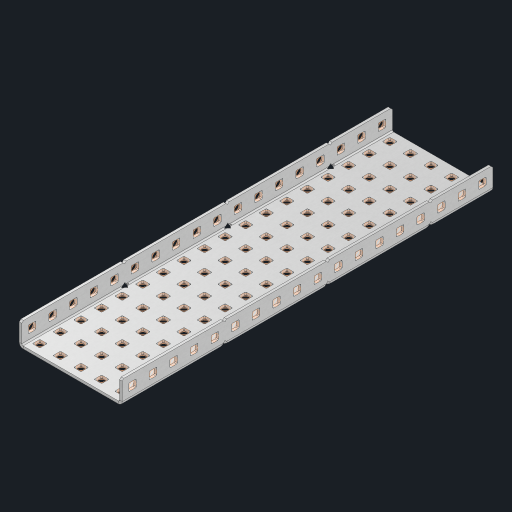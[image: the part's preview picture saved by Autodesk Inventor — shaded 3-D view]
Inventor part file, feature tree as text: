
AUTODESK INVENTOR PART (.ipt)
format: ipt  version: 2023 (Build 270158000, 158)  size: 1,542,144 bytes
history: native  units: in
note: dims shown in document units (in); Inventor stores cm internally (conversion verified against a paired STEP export)
features: other x131, extrude x125, sheet_metal_op x10, sketch x8, mirror x1, pattern_linear x1, chamfer x1
ambient origin geometry x8: Origin, YZ Plane, XZ Plane, XY Plane, X Axis, Y Axis, Z Axis, Center Point
bodies: Solid1 (feature_tree), Body (feature_tree)
feature tree (277):
  other  "Flange Pattern Plane"
  sheet_metal_op  "Flange Pattern"
  sheet_metal_op  "Body Pattern"
  other  "Arc Length"
  mirror  "Notch Mirror"
  pattern_linear  "Notch Pattern"  Spacing1=0.25in  [1 undecoded]
  chamfer  "End Chamfer"
  extrude  "Half Cut"  Depth=0.0625in
  sketch  "Sketch1"  dims[d0=2.5in]
  other  "Plate1"
  sketch  "Sketch2"  dims[d1=9.0in]
  other  "Plate2"
  sheet_metal_op  "Bend1"
  sheet_metal_op  "Corner1"
  sketch  "Sketch3"  dims[d2=0.0625in]
  other  "Flange Pattern Sketch"
  sketch  "Sketch7"  dims[d3=0.0625in]
  other  "Srf1"
  other  "Srf2"
  sketch  "Sketch8"  dims[d4=0.0312in]
  sketch  "Sketch9"  dims[d5=0.125in]
  other  "Srf91"
  sheet_metal_op  "Body Pattern Sketch"
  other  "Srf92"
  sketch  "Sketch13"  dims[d6=0.0625in]
  sketch  "Sketch14"  dims[d7=0.5in d8=90.0deg d9=0.0312in d10=0.25in d11=0.0625in d12=0.0625in d16=0.182in d17=0.02in d18=0.0625in d19=0.0in d20=0.25in d21=0.25in d46=0.172in d47=1.0in d48=0.0in d49=0.182in d50=0.02in d51=0.25in d52=0.25in d53=0.0625in d54=0.0in d55=0.172in d56=1.0in d57=0.0in d60=7.0866in d62=0.5in d63=1.9685in d65=0.5in d85=0.1473in d86=0.1782in d88=0.04in d89=0.0625in d90=0.0in d91=0.04in d92=0.0491in d95=2.5in d96=0.04in d97=0.25in d98=45.0deg d101=0.0in d102=2.497in d131=2.5in d132=7.0866in d134=0.5in d139=0.5in]
  other  "Srf856"
  other  "Srf1310"
  other  "Srf1311"
  other  "Srf1312"
  other  "Srf1376"
  other  "Srf1377"
  other  "Srf1728"
  other  "Srf1755"
  other  "Srf1878"
  other  "Srf1879"
  other  "Srf1880"
  other  "Srf1881"
  other  "Srf1882"
  other  "Srf1883"
  other  "Srf1884"
  other  "Srf1885"
  other  "Srf1886"
  other  "Srf1887"
  other  "Srf1888"
  other  "Srf1889"
  other  "Srf1890"
  other  "Srf1891"
  other  "Srf1892"
  other  "Srf1893"
  other  "Srf1894"
  other  "Srf1895"
  other  "Srf1896"
  other  "Srf1897"
  other  "Srf1898"
  other  "Srf1899"
  other  "Srf1900"
  other  "Srf1901"
  other  "Srf1902"
  other  "Srf1903"
  other  "Srf1904"
  other  "Srf1905"
  other  "Srf1906"
  other  "Srf1942"
  other  "Srf1943"
  other  "Srf1944"
  other  "Srf1945"
  other  "Srf1946"
  other  "Srf1947"
  other  "Srf1948"
  other  "Srf1949"
  other  "Srf1950"
  other  "Srf1951"
  other  "Srf1952"
  other  "Srf1953"
  other  "Srf1954"
  other  "Srf1955"
  other  "Srf1956"
  other  "Srf1957"
  other  "Srf1958"
  other  "Srf1959"
  other  "Srf1960"
  other  "Srf1961"
  other  "Srf1962"
  other  "Srf1963"
  other  "Srf1964"
  other  "Srf1965"
  other  "Srf1966"
  other  "Srf1967"
  other  "Srf1968"
  other  "Srf1969"
  other  "Srf1970"
  other  "Srf2111"
  other  "Srf2146"
  other  "Srf2147"
  other  "Srf2148"
  other  "Srf2149"
  other  "Srf2150"
  other  "Srf2151"
  other  "Srf2152"
  other  "Srf2153"
  other  "Srf2154"
  other  "Srf2155"
  other  "Srf2156"
  other  "Srf2157"
  other  "Srf2158"
  other  "Srf2159"
  other  "Srf2160"
  other  "Srf2161"
  other  "Srf2162"
  other  "Srf2163"
  other  "Srf2164"
  other  "Srf2165"
  other  "Srf2166"
  other  "Srf2167"
  other  "Srf2168"
  other  "Srf2169"
  other  "Srf2170"
  other  "Srf2171"
  other  "Srf2172"
  other  "Srf2173"
  other  "Srf2174"
  other  "Srf2175"
  other  "Srf2176"
  other  "Srf2177"
  other  "Srf2178"
  other  "Srf2179"
  other  "Srf2180"
  other  "Srf2181"
  other  "Srf2182"
  other  "Srf2183"
  other  "Srf2184"
  other  "Srf2185"
  other  "Srf2186"
  other  "Srf2187"
  other  "Srf2188"
  other  "Srf2189"
  other  "Srf2190"
  other  "Srf2191"
  other  "Srf2192"
  other  "Srf2193"
  other  "Srf2194"
  other  "Srf2195"
  other  "Srf2196"
  other  "Srf2197"
  other  "Srf2198"
  other  "Srf2199"
  other  "Srf2200"
  sheet_metal_op  "Flange Stamp"
  sheet_metal_op  "Flange Circle"
  sheet_metal_op  "Body Stamp"
  sheet_metal_op  "Body Circle"
  sheet_metal_op  "Notch"
  extrude  "ExtrusionSrf2"  Depth=0.0625in
  extrude  "ExtrusionSrf92"  Depth=2.5in
  extrude  "ExtrusionSrf856"  Depth=0.02in
  extrude  "ExtrusionSrf1310"  Depth=0.0625in
  extrude  "ExtrusionSrf1311"  TaperAngle=0.0deg  [1 undecoded]
  extrude  "ExtrusionSrf1312"  Depth=0.25in
  extrude  "ExtrusionSrf1376"  Depth=0.25in
  extrude  "ExtrusionSrf1377"  Depth=2.5in
  extrude  "ExtrusionSrf1728"  Depth=2.5in TaperAngle=0.0deg
  extrude  "ExtrusionSrf1755"  Depth=2.5in
  extrude  "ExtrusionSrf1878"  Depth=0.02in
  extrude  "ExtrusionSrf1879"  Depth=0.25in
  extrude  "ExtrusionSrf1880"  Depth=0.25in
  extrude  "ExtrusionSrf1881"  Depth=0.0625in
  extrude  "ExtrusionSrf1882"  TaperAngle=0.0deg  [1 undecoded]
  extrude  "ExtrusionSrf1883"  Depth=2.5in
  extrude  "ExtrusionSrf1884"  Depth=2.5in TaperAngle=0.0deg
  extrude  "ExtrusionSrf1885"  Depth=2.5in
  extrude  "ExtrusionSrf1886"  Depth=2.5in
  extrude  "ExtrusionSrf1887"  Depth=2.5in
  extrude  "ExtrusionSrf1888"  Depth=2.5in
  extrude  "ExtrusionSrf1889"  Depth=2.5in
  extrude  "ExtrusionSrf1890"  Depth=0.0625in
  extrude  "ExtrusionSrf1891"  TaperAngle=0.0deg  [1 undecoded]
  extrude  "ExtrusionSrf1892"  Depth=2.5in
  extrude  "ExtrusionSrf1893"  Depth=2.5in
  extrude  "ExtrusionSrf1894"  Depth=2.5in
  extrude  "ExtrusionSrf1895"  Depth=0.25in TaperAngle=45.0deg
  extrude  "ExtrusionSrf1896"  TaperAngle=0.0deg  [1 undecoded]
  extrude  "ExtrusionSrf1897"  Depth=2.5in
  extrude  "ExtrusionSrf1898"  Depth=2.5in
  extrude  "ExtrusionSrf1899"  Depth=2.5in
  extrude  "ExtrusionSrf1900"  Depth=2.5in
  extrude  "ExtrusionSrf1901"  Depth=2.5in
  extrude  "ExtrusionSrf1902"  [1 undecoded]
  extrude  "ExtrusionSrf1903"  [1 undecoded]
  extrude  "ExtrusionSrf1904"  [1 undecoded]
  extrude  "ExtrusionSrf1905"  [1 undecoded]
  extrude  "ExtrusionSrf1906"  [1 undecoded]
  extrude  "ExtrusionSrf1942"  [1 undecoded]
  extrude  "ExtrusionSrf1943"  [1 undecoded]
  extrude  "ExtrusionSrf1944"  [1 undecoded]
  extrude  "ExtrusionSrf1945"  [1 undecoded]
  extrude  "ExtrusionSrf1946"  [1 undecoded]
  extrude  "ExtrusionSrf1947"  [1 undecoded]
  extrude  "ExtrusionSrf1948"  [1 undecoded]
  extrude  "ExtrusionSrf1949"  [1 undecoded]
  extrude  "ExtrusionSrf1950"  [1 undecoded]
  extrude  "ExtrusionSrf1951"  [1 undecoded]
  extrude  "ExtrusionSrf1952"  [1 undecoded]
  extrude  "ExtrusionSrf1953"  [1 undecoded]
  extrude  "ExtrusionSrf1954"  [1 undecoded]
  extrude  "ExtrusionSrf1955"  [1 undecoded]
  extrude  "ExtrusionSrf1956"  [1 undecoded]
  extrude  "ExtrusionSrf1957"  [1 undecoded]
  extrude  "ExtrusionSrf1958"  [1 undecoded]
  extrude  "ExtrusionSrf1959"  [1 undecoded]
  extrude  "ExtrusionSrf1960"  [1 undecoded]
  extrude  "ExtrusionSrf1961"  [1 undecoded]
  extrude  "ExtrusionSrf1962"  [1 undecoded]
  extrude  "ExtrusionSrf1963"  [1 undecoded]
  extrude  "ExtrusionSrf1964"  [1 undecoded]
  extrude  "ExtrusionSrf1965"  [1 undecoded]
  extrude  "ExtrusionSrf1966"  [1 undecoded]
  extrude  "ExtrusionSrf1967"  [1 undecoded]
  extrude  "ExtrusionSrf1968"  [1 undecoded]
  extrude  "ExtrusionSrf1969"  [1 undecoded]
  extrude  "ExtrusionSrf1970"  [1 undecoded]
  extrude  "ExtrusionSrf2111"  [1 undecoded]
  extrude  "ExtrusionSrf2146"  [1 undecoded]
  extrude  "ExtrusionSrf2147"  [1 undecoded]
  extrude  "ExtrusionSrf2148"  [1 undecoded]
  extrude  "ExtrusionSrf2149"  [1 undecoded]
  extrude  "ExtrusionSrf2150"  [1 undecoded]
  extrude  "ExtrusionSrf2151"  [1 undecoded]
  extrude  "ExtrusionSrf2152"  [1 undecoded]
  extrude  "ExtrusionSrf2153"  [1 undecoded]
  extrude  "ExtrusionSrf2154"  [1 undecoded]
  extrude  "ExtrusionSrf2155"  [1 undecoded]
  extrude  "ExtrusionSrf2156"  [1 undecoded]
  extrude  "ExtrusionSrf2157"  [1 undecoded]
  extrude  "ExtrusionSrf2158"  [1 undecoded]
  extrude  "ExtrusionSrf2159"  [1 undecoded]
  extrude  "ExtrusionSrf2160"  [1 undecoded]
  extrude  "ExtrusionSrf2161"  [1 undecoded]
  extrude  "ExtrusionSrf2162"  [1 undecoded]
  extrude  "ExtrusionSrf2163"  [1 undecoded]
  extrude  "ExtrusionSrf2164"  [1 undecoded]
  extrude  "ExtrusionSrf2165"  [1 undecoded]
  extrude  "ExtrusionSrf2166"  [1 undecoded]
  extrude  "ExtrusionSrf2167"  [1 undecoded]
  extrude  "ExtrusionSrf2168"  [1 undecoded]
  extrude  "ExtrusionSrf2169"  [1 undecoded]
  extrude  "ExtrusionSrf2170"  [1 undecoded]
  extrude  "ExtrusionSrf2171"  [1 undecoded]
  extrude  "ExtrusionSrf2172"  [1 undecoded]
  extrude  "ExtrusionSrf2173"  [1 undecoded]
  extrude  "ExtrusionSrf2174"  [1 undecoded]
  extrude  "ExtrusionSrf2175"  [1 undecoded]
  extrude  "ExtrusionSrf2176"  [1 undecoded]
  extrude  "ExtrusionSrf2177"  [1 undecoded]
  extrude  "ExtrusionSrf2178"  [1 undecoded]
  extrude  "ExtrusionSrf2179"  [1 undecoded]
  extrude  "ExtrusionSrf2180"  [1 undecoded]
  extrude  "ExtrusionSrf2181"  [1 undecoded]
  extrude  "ExtrusionSrf2182"  [1 undecoded]
  extrude  "ExtrusionSrf2183"  [1 undecoded]
  extrude  "ExtrusionSrf2184"  [1 undecoded]
  extrude  "ExtrusionSrf2185"  [1 undecoded]
  extrude  "ExtrusionSrf2186"  [1 undecoded]
  extrude  "ExtrusionSrf2187"  [1 undecoded]
  extrude  "ExtrusionSrf2188"  [1 undecoded]
  extrude  "ExtrusionSrf2189"  [1 undecoded]
  extrude  "ExtrusionSrf2190"  [1 undecoded]
  extrude  "ExtrusionSrf2191"  [1 undecoded]
  extrude  "ExtrusionSrf2192"  [1 undecoded]
  extrude  "ExtrusionSrf2193"  [1 undecoded]
  extrude  "ExtrusionSrf2194"  [1 undecoded]
  extrude  "ExtrusionSrf2195"  [1 undecoded]
  extrude  "ExtrusionSrf2196"  [1 undecoded]
  extrude  "ExtrusionSrf2197"  [1 undecoded]
  extrude  "ExtrusionSrf2198"  [1 undecoded]
  extrude  "ExtrusionSrf2199"  [1 undecoded]
  extrude  "ExtrusionSrf2200"  [1 undecoded]
note: 95 required parameter values undecoded (feature->parameter linkage not recoverable at this tier; creation-order binding heuristic only, values carry confidence <= 0.55)
